annotation { "Feature Type Name" : "Feature", "Feature Type Description" : "" }
export const myFeature = defineFeature(function(context is Context, id is Id, definition is map)
    precondition{}
    {
        {
            var Q0;
            Q0=qCreatedBy(makeId("Top.planeOp"),FACE);
            var sketch = newSketch(context, id + "F0", { "sketchPlane" : qUnion([Q0])});
            skCircle(sketch, "E0.cCircle", {"center": v(0, 0) * mm, "radius": 56.65 * mm, "construction": true});
            skLineSegment(sketch, "E0.0", {"start": v(-60.7, 8.65) * mm, "end": v(-36.8, 49.04) * mm});
            skLineSegment(sketch, "E0.1", {"start": v(-36.8, 49.04) * mm, "end": v(8.65, 60.7) * mm});
            skLineSegment(sketch, "E0.2", {"start": v(8.65, 60.7) * mm, "end": v(49.04, 36.8) * mm});
            skLineSegment(sketch, "E0.3", {"start": v(49.04, 36.8) * mm, "end": v(60.7, -8.65) * mm});
            skLineSegment(sketch, "E0.4", {"start": v(60.7, -8.65) * mm, "end": v(36.8, -49.04) * mm});
            skLineSegment(sketch, "E0.5", {"start": v(36.8, -49.04) * mm, "end": v(-8.65, -60.7) * mm});
            skLineSegment(sketch, "E0.6", {"start": v(-8.65, -60.7) * mm, "end": v(-49.04, -36.8) * mm});
            skLineSegment(sketch, "E0.7", {"start": v(-49.04, -36.8) * mm, "end": v(-60.7, 8.65) * mm});
            skPoint(sketch, "E0.0.midPoint", {"position": v(-48.75, 28.85) * mm});
            skSolve(sketch);
        }
        {
            var Q0;
            Q0=makeQuery(id+"F0.imprint","IMPRINT",FACE,{"disambiguationData":[TD([[makeQuery(id+"F0.imprint","IMPRINT",EDGE,{"derivedFrom":sQuery(id+"F0.wireOp",EDGE,"E0.0")}),-1.0]])]});
            extrude(context, id + "F1", {"entities" : qUnion([Q0]), "depth" : 6.35 * mm});
        }
        {
            var Q0;
            Q0=makeQuery(id+"F1.opExtrude","CAP_FACE",FACE,{"disambiguationData":[OSD([sQuery(id+"F0.wireOp",EDGE,"E0.0"),sQuery(id+"F0.wireOp",EDGE,"E0.1"),sQuery(id+"F0.wireOp",EDGE,"E0.2"),sQuery(id+"F0.wireOp",EDGE,"E0.3"),sQuery(id+"F0.wireOp",EDGE,"E0.4"),sQuery(id+"F0.wireOp",EDGE,"E0.5"),sQuery(id+"F0.wireOp",EDGE,"E0.6"),sQuery(id+"F0.wireOp",EDGE,"E0.7")])],"isStart":false});
            var sketch = newSketch(context, id + "F2", { "sketchPlane" : qUnion([Q0])});
            skText(sketch, "E1", { "text": "Puddin\'", "fontName": "NotoSansCJKjp-Bold.otf"});
            const initialGuessF2  = {"E1": [-0.04075, -0.00715, 1, 0, 0.01505]};
            skSetInitialGuess(sketch, initialGuessF2);
            skSolve(sketch);
        }
        {
            var Q0;
            Q0 = qSketchRegion(id + "F2", true);
            extrude(context, id + "F3", {"entities" : qUnion([Q0]), "operationType" : NewBodyOperationType.REMOVE, "oppositeDirection" : true, "depth" : 3.05 * mm});
        }
        {
            var Q0;
            Q0=qCreatedBy(makeId("Top.planeOp"),FACE);
            var sketch = newSketch(context, id + "F4", { "sketchPlane" : qUnion([Q0])});
            skCircle(sketch, "E2", {"center": v(0, 46.35) * mm, "radius": 6.04 * mm});
            skSolve(sketch);
        }
        {
            var Q0;
            Q0=sQuery(id+"F4.wireOp",VERTEX,"E2.center");
            var Q1;
            Q1=makeQuery(id+"F1.opExtrude","SWEPT_BODY",BODY,{"disambiguationData":[OSD([sQuery(id+"F0.wireOp",EDGE,"E0.0"),sQuery(id+"F0.wireOp",EDGE,"E0.1"),sQuery(id+"F0.wireOp",EDGE,"E0.2"),sQuery(id+"F0.wireOp",EDGE,"E0.3"),sQuery(id+"F0.wireOp",EDGE,"E0.4"),sQuery(id+"F0.wireOp",EDGE,"E0.5"),sQuery(id+"F0.wireOp",EDGE,"E0.6"),sQuery(id+"F0.wireOp",EDGE,"E0.7")])]});
            hole(context, id + "F5", {"style" : HoleStyle.SIMPLE, "endStyle" : HoleEndStyle.THROUGH, "oppositeDirection" : true, "holeDiameter" : 12.7 * mm, "locations" : qUnion([Q0]), "scope" : qUnion([Q1]), "isTappedThrough" : true});
        }
        {
            var Q0;
            {var subQ0=sQuery(id+"F0.wireOp",EDGE,"E0.7");var subQ1=sQuery(id+"F0.wireOp",EDGE,"E0.6");var subQ2=sQuery(id+"F0.wireOp",EDGE,"E0.4");var subQ3=sQuery(id+"F0.wireOp",EDGE,"E0.5");var subQ4=sQuery(id+"F0.wireOp",EDGE,"E0.1");var subQ5=sQuery(id+"F0.wireOp",EDGE,"E0.2");var subQ6=sQuery(id+"F0.wireOp",EDGE,"E0.3");var subQ7=sQuery(id+"F0.wireOp",EDGE,"E0.0");Q0=makeQuery(id+"F3.boolean.opBoolean","SPLIT",FACE,{"disambiguationData":[TD([makeQuery(id+"F1.opExtrude","SWEPT_FACE",FACE,{"disambiguationData":[OSD([subQ7])]})])],"derivedFrom":makeQuery(id+"F1.opExtrude","CAP_FACE",FACE,{"disambiguationData":[OSD([subQ7,subQ4,subQ5,subQ6,subQ2,subQ3,subQ1,subQ0])],"isStart":false})});}
            var sketch = newSketch(context, id + "F6", { "sketchPlane" : qUnion([Q0])});
            skText(sketch, "E3", { "text": "Jeremiah Jones", "fontName": "DroidSansMono.ttf"});
            const initialGuessF6  = {"E3": [-0.02864, -0.02638, 1, 0, 0.00486]};
            skSetInitialGuess(sketch, initialGuessF6);
            skSolve(sketch);
        }
        {
            var Q0;
            Q0 = qSketchRegion(id + "F6", true);
            extrude(context, id + "F7", {"entities" : qUnion([Q0]), "operationType" : NewBodyOperationType.REMOVE, "oppositeDirection" : true, "depth" : 3.05 * mm});
        }
        {
            var Q0;
            {var subQ16=sQuery(id+"F0.wireOp",EDGE,"E0.1");var subQ22=sQuery(id+"F0.wireOp",EDGE,"E0.3");var subQ26=sQuery(id+"F0.wireOp",EDGE,"E0.2");var subQ40=sQuery(id+"F0.wireOp",EDGE,"E0.7");var subQ45=sQuery(id+"F0.wireOp",EDGE,"E0.6");var subQ51=sQuery(id+"F0.wireOp",EDGE,"E0.5");var subQ53=sQuery(id+"F0.wireOp",EDGE,"E0.4");var subQ56=sQuery(id+"F0.wireOp",EDGE,"E0.0");var subQ57=makeQuery(id+"F1.opExtrude","SWEPT_FACE",FACE,{"disambiguationData":[OSD([subQ56])]});Q0=makeQuery(id+"F7.boolean.opBoolean","SPLIT",FACE,{"disambiguationData":[TD([subQ57])],"derivedFrom":makeQuery(id+"F3.boolean.opBoolean","SPLIT",FACE,{"disambiguationData":[TD([subQ57])],"derivedFrom":makeQuery(id+"F1.opExtrude","CAP_FACE",FACE,{"disambiguationData":[OSD([subQ56,subQ16,subQ26,subQ22,subQ53,subQ51,subQ45,subQ40])],"isStart":false})})});}
            var sketch = newSketch(context, id + "F8", { "sketchPlane" : qUnion([Q0])});
            skText(sketch, "E4", { "text": "931-209-0982", "fontName": "DroidSansMono.ttf"});
            const initialGuessF8  = {"E4": [-0.02534, -0.03471, 1, 0, 0.00503]};
            skSetInitialGuess(sketch, initialGuessF8);
            skSolve(sketch);
        }
        {
            var Q0;
            Q0 = qSketchRegion(id + "F8", true);
            extrude(context, id + "F9", {"entities" : qUnion([Q0]), "operationType" : NewBodyOperationType.REMOVE, "oppositeDirection" : true, "depth" : 3.05 * mm});
        }
        {
            var Q0;
            {var subQ11=sQuery(id+"F0.wireOp",EDGE,"E0.3");var subQ134=sQuery(id+"F0.wireOp",EDGE,"E0.1");var subQ146=sQuery(id+"F0.wireOp",EDGE,"E0.2");var subQ167=sQuery(id+"F0.wireOp",EDGE,"E0.7");var subQ177=sQuery(id+"F0.wireOp",EDGE,"E0.6");var subQ185=sQuery(id+"F0.wireOp",EDGE,"E0.5");var subQ191=sQuery(id+"F0.wireOp",EDGE,"E0.0");var subQ192=makeQuery(id+"F1.opExtrude","SWEPT_FACE",FACE,{"disambiguationData":[OSD([subQ191])]});var subQ223=sQuery(id+"F0.wireOp",EDGE,"E0.4");Q0=makeQuery(id+"F9.boolean.opBoolean","SPLIT",FACE,{"disambiguationData":[TD([subQ192])],"derivedFrom":makeQuery(id+"F7.boolean.opBoolean","SPLIT",FACE,{"disambiguationData":[TD([subQ192])],"derivedFrom":makeQuery(id+"F3.boolean.opBoolean","SPLIT",FACE,{"disambiguationData":[TD([subQ192])],"derivedFrom":makeQuery(id+"F1.opExtrude","CAP_FACE",FACE,{"disambiguationData":[OSD([subQ191,subQ134,subQ146,subQ11,subQ223,subQ185,subQ177,subQ167])],"isStart":false})})})});}
            var sketch = newSketch(context, id + "F10", { "sketchPlane" : qUnion([Q0])});
            skText(sketch, "E5", { "text": "414 Hillcrest Drive\nNew Johnsonville, TN", "fontName": "OpenSans-Regular.ttf"});
            const initialGuessF10  = {"E5": [-0.02343, -0.04148, 1, 0, 0.00347]};
            skSetInitialGuess(sketch, initialGuessF10);
            skSolve(sketch);
        }
        {
            var Q0;
            Q0 = qSketchRegion(id + "F10", true);
            extrude(context, id + "F11", {"entities" : qUnion([Q0]), "operationType" : NewBodyOperationType.REMOVE, "oppositeDirection" : true, "depth" : 3.05 * mm});
        }
        {
            var Q0;
            {var subQ85=sQuery(id+"F0.wireOp",EDGE,"E0.3");var subQ176=sQuery(id+"F0.wireOp",EDGE,"E0.1");var subQ204=sQuery(id+"F0.wireOp",EDGE,"E0.5");var subQ273=sQuery(id+"F0.wireOp",EDGE,"E0.4");var subQ313=sQuery(id+"F0.wireOp",EDGE,"E0.7");var subQ326=sQuery(id+"F0.wireOp",EDGE,"E0.6");var subQ345=sQuery(id+"F0.wireOp",EDGE,"E0.0");var subQ346=makeQuery(id+"F1.opExtrude","SWEPT_FACE",FACE,{"disambiguationData":[OSD([subQ345])]});var subQ417=sQuery(id+"F0.wireOp",EDGE,"E0.2");Q0=makeQuery(id+"F11.boolean.opBoolean","SPLIT",FACE,{"disambiguationData":[TD([subQ346])],"derivedFrom":makeQuery(id+"F9.boolean.opBoolean","SPLIT",FACE,{"disambiguationData":[TD([subQ346])],"derivedFrom":makeQuery(id+"F7.boolean.opBoolean","SPLIT",FACE,{"disambiguationData":[TD([subQ346])],"derivedFrom":makeQuery(id+"F3.boolean.opBoolean","SPLIT",FACE,{"disambiguationData":[TD([subQ346])],"derivedFrom":makeQuery(id+"F1.opExtrude","CAP_FACE",FACE,{"disambiguationData":[OSD([subQ345,subQ176,subQ417,subQ85,subQ273,subQ204,subQ326,subQ313])],"isStart":false})})})})});}
            var sketch = newSketch(context, id + "F12", { "sketchPlane" : qUnion([Q0])});
            skFitSpline(sketch, "E6", {"points": [v(-13.7, 29.87) * mm, v(12.5, 29.7) * mm, v(14.59, 34.21) * mm, v(20.84, 34.73) * mm, v(22.4, 29.87) * mm, v(19.45, 26.92) * mm, v(23.79, 22.93) * mm, v(21.53, 18.6) * mm, v(16.67, 18.94) * mm, v(14.24, 21.2) * mm, v(-13.7, 22.4) * mm, v(-16.48, 21.37) * mm, v(-20.47, 19.98) * mm, v(-23.77, 25.7) * mm, v(-18.04, 26.23) * mm, v(-24.98, 30.57) * mm, v(-21.16, 34.21) * mm, v(-17.52, 31.78) * mm, v(-13.7, 29.87) * mm]});
            skSolve(sketch);
        }
        {
            var Q0;
            Q0 = qSketchRegion(id + "F12", true);
            extrude(context, id + "F13", {"entities" : qUnion([Q0]), "operationType" : NewBodyOperationType.REMOVE, "oppositeDirection" : true, "depth" : 12.7 * mm});
        }
    });